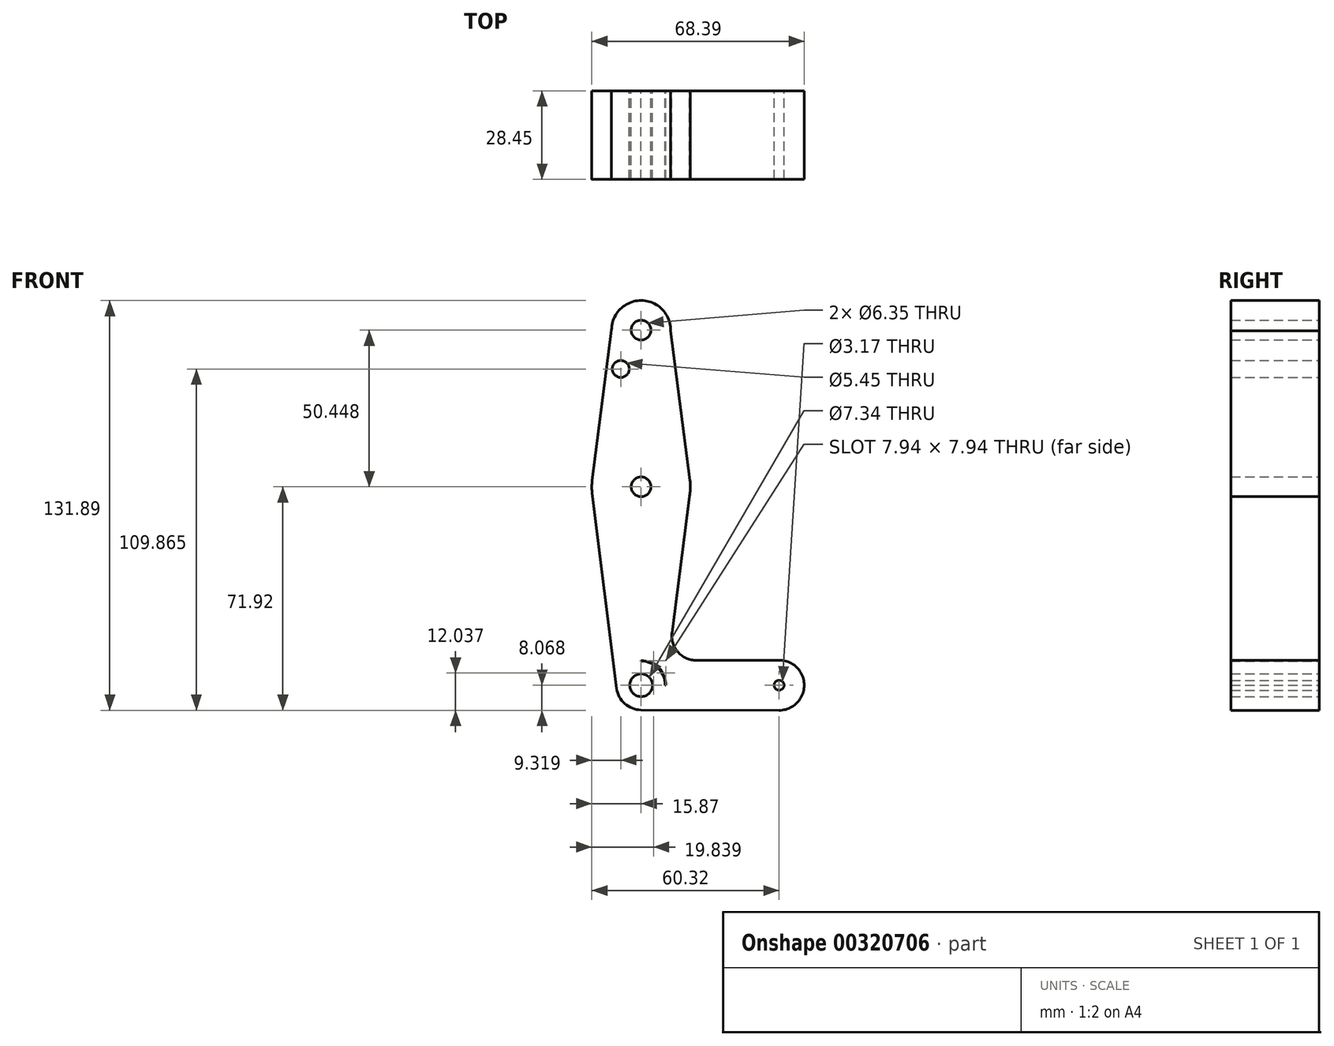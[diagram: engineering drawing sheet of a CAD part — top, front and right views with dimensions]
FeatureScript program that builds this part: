
annotation { "Feature Type Name" : "Feature", "Feature Type Description" : "" }
export const myFeature = defineFeature(function(context is Context, id is Id, definition is map)
    precondition{}
    {
        {
            var Q0;
            Q0=qCreatedBy(makeId("Front.planeOp"),FACE);
            var sketch = newSketch(context, id + "F0", { "sketchPlane" : qUnion([Q0])});
            skLineSegment(sketch, "E0", {"start": v(-31.23, 50.45) * mm, "end": v(-31.23, -63.85) * mm});
            skLineSegment(sketch, "E1", {"start": v(-31.23, -63.85) * mm, "end": v(13.22, -63.85) * mm});
            skCircle(sketch, "E2", {"center": v(-31.23, 50.45) * mm, "radius": 9.53 * mm});
            skCircle(sketch, "E3", {"center": v(-31.23, 0) * mm, "radius": 15.88 * mm});
            skCircle(sketch, "E4", {"center": v(-31.23, -63.85) * mm, "radius": 7.94 * mm});
            skCircle(sketch, "E5", {"center": v(13.22, -63.85) * mm, "radius": 8.07 * mm});
            skLineSegment(sketch, "E6", {"start": v(-40.75, 50.45) * mm, "end": v(-47.24, 0) * mm});
            skLineSegment(sketch, "E7", {"start": v(-47, -1.83) * mm, "end": v(-39.1, -64.84) * mm});
            skLineSegment(sketch, "E8", {"start": v(-21.7, 50.25) * mm, "end": v(-15.22, 0) * mm});
            skLineSegment(sketch, "E9", {"start": v(-15.38, -0.87) * mm, "end": v(-21.3, -46.9) * mm});
            skLineSegment(sketch, "E10", {"start": v(-31.25, -71.79) * mm, "end": v(13.2, -71.92) * mm});
            skLineSegment(sketch, "E11", {"start": v(13.22, -55.78) * mm, "end": v(-13.38, -55.86) * mm});
            skPoint(sketch, "E12.newPointA", {"position": v(-23.47, -63.85) * mm});
            skArc(sketch, "E12.filletArc", {"start": v(-21.3, -46.9) * mm, "mid": v(-19.37, -53.17) * mm, "end": v(-13.38, -55.86) * mm});
            skCircle(sketch, "E13", {"center": v(-31.23, 50.45) * mm, "radius": 3.18 * mm});
            skCircle(sketch, "E14", {"center": v(-37.78, 37.94) * mm, "radius": 2.73 * mm});
            skCircle(sketch, "E15", {"center": v(-31.23, 0) * mm, "radius": 3.18 * mm});
            skCircle(sketch, "E16", {"center": v(-31.23, -63.85) * mm, "radius": 1.59 * mm});
            skCircle(sketch, "E17", {"center": v(13.22, -63.85) * mm, "radius": 1.59 * mm});
            skCircle(sketch, "E18", {"center": v(-31.23, -63.85) * mm, "radius": 7.76 * mm});
            skCircle(sketch, "E19", {"center": v(-31.23, -63.85) * mm, "radius": 3.67 * mm});
            skSolve(sketch);
        }
        {
            var Q0;
            Q0 = qSketchRegion(id + "F0", true);
            var Q1;
            {var subQ0=sQuery(id+"F0.wireOp",EDGE,"E18");var subQ1=sQuery(id+"F0.wireOp",EDGE,"E0");var subQ2=makeQuery(id+"F0.imprint","INTERSECT",VERTEX,{"derivedFrom":[subQ1,subQ0]});Q1=makeQuery(id+"F0.imprint","IMPRINT",FACE,{"disambiguationData":[TD([[makeQuery(id+"F0.imprint","IMPRINT",EDGE,{"disambiguationData":[TD([[subQ2,-1.0]])],"derivedFrom":subQ1}),-1.0]])]});}
            var Q2;
            {var subQ0=sQuery(id+"F0.wireOp",EDGE,"E18");var subQ1=sQuery(id+"F0.wireOp",EDGE,"E0");var subQ2=makeQuery(id+"F0.imprint","INTERSECT",VERTEX,{"derivedFrom":[subQ1,subQ0]});Q2=makeQuery(id+"F0.imprint","IMPRINT",FACE,{"disambiguationData":[TD([[makeQuery(id+"F0.imprint","IMPRINT",EDGE,{"disambiguationData":[TD([[subQ2,-1.0]])],"derivedFrom":subQ1}),1.0]])]});}
            extrude(context, id + "F1", {"entities" : qUnion([Q0, Q1, Q2]), "depth" : 28.45 * mm});
        }
    });
